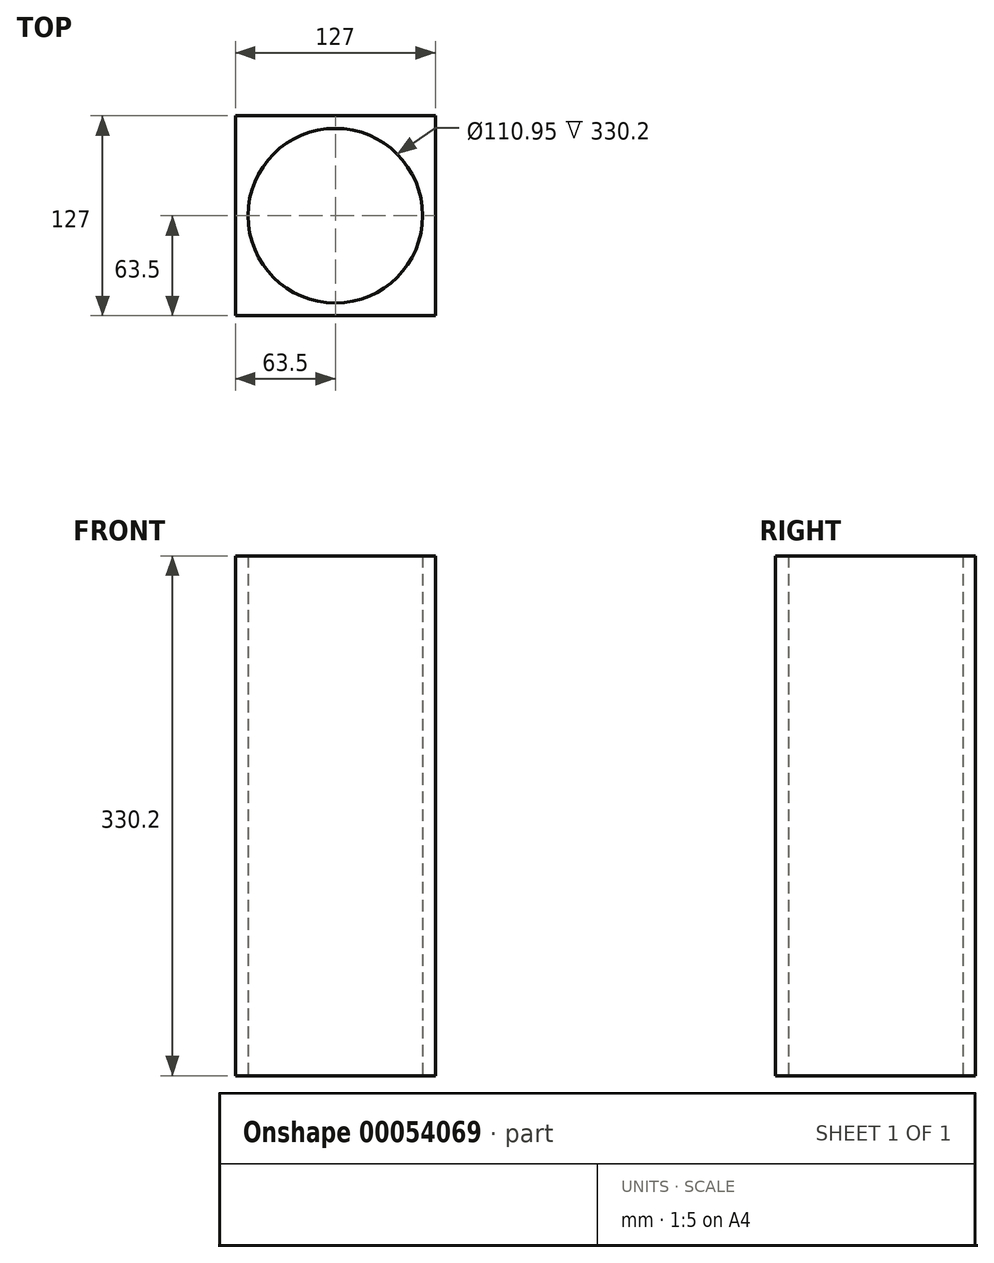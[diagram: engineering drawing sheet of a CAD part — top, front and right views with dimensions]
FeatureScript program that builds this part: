
annotation { "Feature Type Name" : "Feature", "Feature Type Description" : "" }
export const myFeature = defineFeature(function(context is Context, id is Id, definition is map)
    precondition{}
    {
        {
            var Q0;
            Q0=qCreatedBy(makeId("Top.planeOp"),FACE);
            var sketch = newSketch(context, id + "F0", { "sketchPlane" : qUnion([Q0])});
            skLineSegment(sketch, "E0.bottom", {"start": v(0, 0) * mm, "end": v(-127, 0) * mm});
            skLineSegment(sketch, "E0.top", {"start": v(0, 127) * mm, "end": v(-127, 127) * mm});
            skLineSegment(sketch, "E0.left", {"start": v(0, 0) * mm, "end": v(0, 127) * mm});
            skLineSegment(sketch, "E0.right", {"start": v(-127, 0) * mm, "end": v(-127, 127) * mm});
            skLineSegment(sketch, "E1", {"start": v(-127, 127) * mm, "end": v(0, 0) * mm, "construction": true});
            skCircle(sketch, "E2", {"center": v(-63.5, 63.5) * mm, "radius": 55.48 * mm});
            skSolve(sketch);
        }
        {
            var Q0;
            Q0 = qSketchRegion(id + "F0", true);
            extrude(context, id + "F1", {"entities" : qUnion([Q0]), "depth" : 330.2 * mm});
        }
        {
            var Q0;
            Q0=makeQuery(id+"F0.imprint","IMPRINT",FACE,{"disambiguationData":[TD([[makeQuery(id+"F0.imprint","IMPRINT",EDGE,{"derivedFrom":sQuery(id+"F0.wireOp",EDGE,"E2")}),1.0]])]});
            extrude(context, id + "F2", {"entities" : qUnion([Q0]), "operationType" : NewBodyOperationType.REMOVE, "endBound" : BoundingType.THROUGH_ALL, "depth" : 25.4 * mm});
        }
    });
